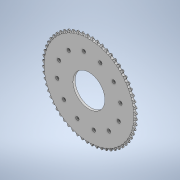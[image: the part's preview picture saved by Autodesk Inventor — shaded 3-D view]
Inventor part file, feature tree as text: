
AUTODESK INVENTOR PART (.ipt)
format: ipt  version: 2020 (Build 240168000, 168)  size: 1,419,776 bytes
history: native  units: in
note: dims shown in document units (in); Inventor stores cm internally (conversion verified against a paired STEP export)
features: extrude x1, sketch x1, boolean_combine x1
ambient origin geometry x8: Origin, YZ Plane, XZ Plane, XY Plane, X Axis, Y Axis, Z Axis, Center Point
bodies: Solid1 (feature_tree)
feature tree (3):
  extrude  "Extrusion1"  Depth=0.3937in
  sketch  "Sketch1"  dims[d0=2.5in d1=0.2656in d2=2.5in d3=4.7244in d5=0.0in d7=4.7244in d9=0.0in d11=4.7244in d13=360.0deg d15=0.3937in d16=0.0in]
  boolean_combine  "Combine2"
